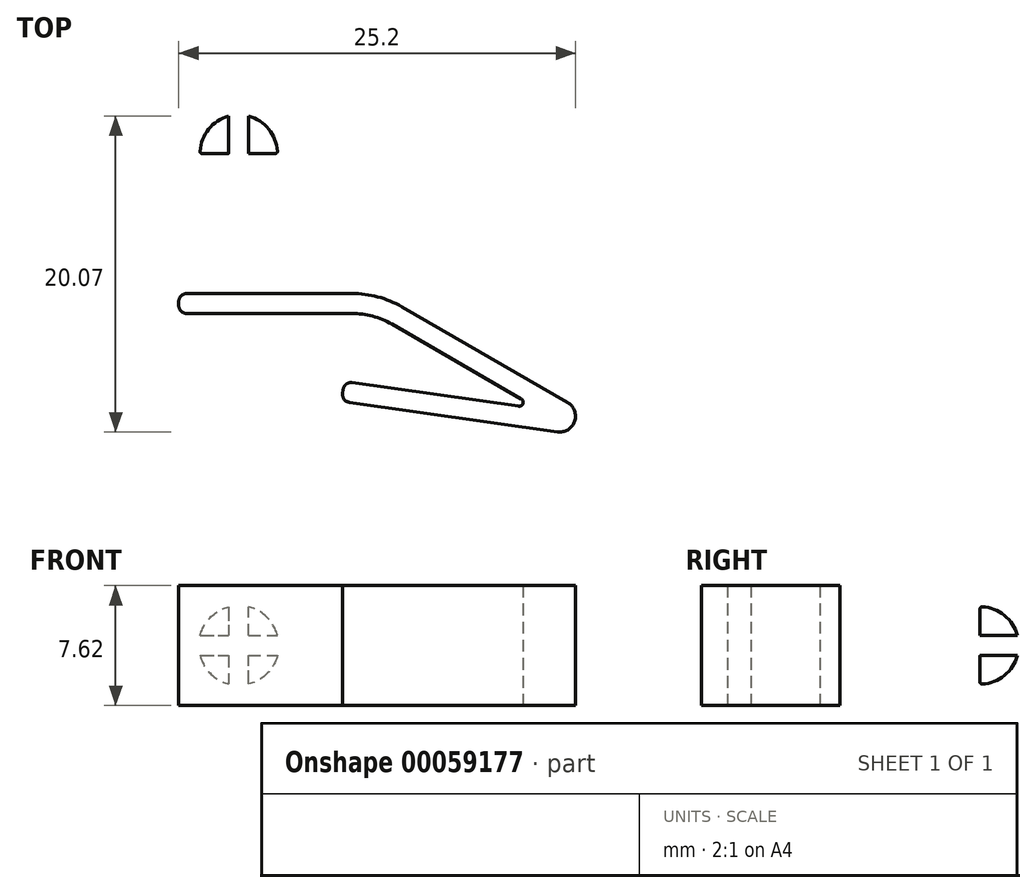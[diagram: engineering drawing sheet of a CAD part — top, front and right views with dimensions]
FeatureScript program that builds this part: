
annotation { "Feature Type Name" : "Feature", "Feature Type Description" : "" }
export const myFeature = defineFeature(function(context is Context, id is Id, definition is map)
    precondition{}
    {
        {
            var Q0;
            Q0=qCreatedBy(makeId("Top.planeOp"),FACE);
            var sketch = newSketch(context, id + "F0", { "sketchPlane" : qUnion([Q0])});
            skLineSegment(sketch, "E0", {"start": v(0.5, 0) * mm, "end": v(11, 0) * mm});
            skLineSegment(sketch, "E1", {"start": v(14.17, -0.85) * mm, "end": v(24.7, -6.93) * mm});
            skLineSegment(sketch, "E2", {"start": v(24.05, -8.8) * mm, "end": v(10.84, -6.92) * mm});
            skPoint(sketch, "E3.visualSharp", {"position": v(12.7, 0) * mm});
            skArc(sketch, "E3.filletArc", {"start": v(14.17, -0.85) * mm, "mid": v(12.64, -0.22) * mm, "end": v(11, 0) * mm});
            skPoint(sketch, "E4.visualSharp", {"position": v(29.2, -9.52) * mm});
            skArc(sketch, "E4.filletArc", {"start": v(24.05, -8.8) * mm, "mid": v(25.14, -8.13) * mm, "end": v(24.7, -6.93) * mm});
            skLineSegment(sketch, "E5.0", {"start": v(21.59, -7.16) * mm, "end": v(11.02, -5.66) * mm});
            skLineSegment(sketch, "E5.1", {"start": v(13.54, -1.95) * mm, "end": v(21.75, -6.7) * mm});
            skArc(sketch, "E5.2", {"start": v(13.54, -1.95) * mm, "mid": v(12.31, -1.44) * mm, "end": v(11, -1.27) * mm});
            skLineSegment(sketch, "E5.3", {"start": v(0.5, -1.27) * mm, "end": v(11, -1.27) * mm});
            skPoint(sketch, "E6.visualSharp", {"position": v(22.88, -7.35) * mm});
            skArc(sketch, "E6.filletArc", {"start": v(21.59, -7.16) * mm, "mid": v(21.86, -7) * mm, "end": v(21.75, -6.7) * mm});
            skLineSegment(sketch, "E7", {"start": v(0, -0.5) * mm, "end": v(0, -0.76) * mm});
            skLineSegment(sketch, "E8", {"start": v(10.44, -6.1) * mm, "end": v(10.4, -6.34) * mm});
            skPoint(sketch, "E9.visualSharp", {"position": v(10.52, -5.6) * mm});
            skArc(sketch, "E9.filletArc", {"start": v(11.02, -5.66) * mm, "mid": v(10.64, -5.76) * mm, "end": v(10.44, -6.1) * mm});
            skPoint(sketch, "E10.visualSharp", {"position": v(10.34, -6.85) * mm});
            skArc(sketch, "E10.filletArc", {"start": v(10.4, -6.34) * mm, "mid": v(10.5, -6.72) * mm, "end": v(10.84, -6.92) * mm});
            skPoint(sketch, "E11.visualSharp", {"position": v(0, 0) * mm});
            skArc(sketch, "E11.filletArc", {"start": v(0.5, 0) * mm, "mid": v(0.15, -0.15) * mm, "end": v(0, -0.5) * mm});
            skPoint(sketch, "E12.visualSharp", {"position": v(0, -1.27) * mm});
            skArc(sketch, "E12.filletArc", {"start": v(0, -0.76) * mm, "mid": v(0.15, -1.12) * mm, "end": v(0.5, -1.27) * mm});
            skSolve(sketch);
        }
        {
            var Q0;
            Q0=makeQuery(id+"F0.imprint","IMPRINT",FACE,{"disambiguationData":[TD([[makeQuery(id+"F0.imprint","IMPRINT",EDGE,{"derivedFrom":sQuery(id+"F0.wireOp",EDGE,"E0")}),-1.0]])]});
            extrude(context, id + "F1", {"entities" : qUnion([Q0]), "depth" : 7.62 * mm});
        }
        {
            var Q0;
            Q0=makeQuery(id+"F1.opExtrude","CAP_FACE",FACE,{"disambiguationData":[OSD([sQuery(id+"F0.wireOp",EDGE,"E0"),sQuery(id+"F0.wireOp",EDGE,"E1"),sQuery(id+"F0.wireOp",EDGE,"E2"),sQuery(id+"F0.wireOp",EDGE,"E3.filletArc"),sQuery(id+"F0.wireOp",EDGE,"E4.filletArc"),sQuery(id+"F0.wireOp",EDGE,"E5.0"),sQuery(id+"F0.wireOp",EDGE,"E5.1"),sQuery(id+"F0.wireOp",EDGE,"E5.2"),sQuery(id+"F0.wireOp",EDGE,"E5.3"),sQuery(id+"F0.wireOp",EDGE,"E6.filletArc"),sQuery(id+"F0.wireOp",EDGE,"E7"),sQuery(id+"F0.wireOp",EDGE,"E8"),sQuery(id+"F0.wireOp",EDGE,"E9.filletArc"),sQuery(id+"F0.wireOp",EDGE,"E10.filletArc"),sQuery(id+"F0.wireOp",EDGE,"E11.filletArc"),sQuery(id+"F0.wireOp",EDGE,"E12.filletArc")])],"isStart":false});
            cPlane(context, id + "F2", {"entities" : qUnion([Q0]), "cplaneType" : CPlaneType.OFFSET, "offset" : 3.8 * mm, "oppositeDirection" : true, "width" : 152.4 * mm, "height" : 152.4 * mm});
        }
        {
            var Q0;
            Q0=qCreatedBy(id+"F2.planeOp",FACE);
            var sketch = newSketch(context, id + "F3", { "sketchPlane" : qUnion([Q0])});
            skLineSegment(sketch, "E13", {"start": v(3.81, 0) * mm, "end": v(3.81, 8.9) * mm});
            skLineSegment(sketch, "E14", {"start": v(3.8, 8.9) * mm, "end": v(5.84, 8.9) * mm});
            skLineSegment(sketch, "E15", {"start": v(5.84, 8.9) * mm, "end": v(5.84, 0) * mm});
            skLineSegment(sketch, "E16", {"start": v(3.81, 0) * mm, "end": v(5.84, 0) * mm});
            skLineSegment(sketch, "E17", {"start": v(5.84, 8.9) * mm, "end": v(6.35, 8.9) * mm});
            skLineSegment(sketch, "E18", {"start": v(3.81, 8.9) * mm, "end": v(3.81, 12.2) * mm});
            skLineSegment(sketch, "E19.bottom", {"start": v(3.8, 3.05) * mm, "end": v(4.44, 3.05) * mm});
            skLineSegment(sketch, "E19.top", {"start": v(3.8, 12.2) * mm, "end": v(4.44, 12.2) * mm});
            skLineSegment(sketch, "E19.left", {"start": v(3.81, 3.05) * mm, "end": v(3.81, 12.2) * mm});
            skLineSegment(sketch, "E19.right", {"start": v(4.44, 3.05) * mm, "end": v(4.44, 12.2) * mm});
            skArc(sketch, "E20", {"start": v(6.35, 8.9) * mm, "mid": v(5.6, 10.69) * mm, "end": v(3.81, 11.43) * mm});
            skSolve(sketch);
        }
        {
            var Q0;
            Q0=makeQuery(id+"F3.imprint","IMPRINT",FACE,{"disambiguationData":[TD([[makeQuery(id+"F3.imprint","IMPRINT",EDGE,{"derivedFrom":sQuery(id+"F3.wireOp",EDGE,"E13")}),-1.0]])]});
            var Q1;
            {var subQ0=sQuery(id+"F3.wireOp",EDGE,"E17");Q1=makeQuery(id+"F3.imprint","IMPRINT",FACE,{"disambiguationData":[TD([[makeQuery(id+"F3.imprint","IMPRINT",EDGE,{"derivedFrom":subQ0}),1.0]])]});}
            var Q2;
            {var subQ0=sQuery(id+"F3.wireOp",EDGE,"E19.left");var subQ1=sQuery(id+"F3.wireOp",EDGE,"E14");var subQ2=makeQuery(id+"F3.imprint","INTERSECT",VERTEX,{"derivedFrom":[subQ1,subQ0]});Q2=makeQuery(id+"F3.imprint","IMPRINT",FACE,{"disambiguationData":[TD([[makeQuery(id+"F3.imprint","IMPRINT",EDGE,{"disambiguationData":[TD([[subQ2,-1.0]])],"derivedFrom":subQ1}),1.0]])]});}
            var Q3;
            {var subQ5=sQuery(id+"F3.wireOp",EDGE,"E19.bottom");Q3=makeQuery(id+"F3.imprint","IMPRINT",FACE,{"disambiguationData":[TD([[makeQuery(id+"F3.imprint","IMPRINT",EDGE,{"derivedFrom":subQ5}),1.0]])]});}
            var Q4;
            Q4=sQuery(id+"F3.wireOp",EDGE,"E13");
            revolve(context, id + "F4", {"operationType" : NewBodyOperationType.ADD, "entities" : qUnion([Q0, Q1, Q2, Q3]), "axis" : qUnion([Q4]), "revolveType" : RevolveType.FULL});
        }
        {
            var Q0;
            Q0=qCreatedBy(id+"F2.planeOp",FACE);
            var sketch = newSketch(context, id + "F5", { "sketchPlane" : qUnion([Q0])});
            skLineSegment(sketch, "E21.7", {"start": v(3.8, 3.05) * mm, "end": v(4.44, 3.05) * mm});
            skLineSegment(sketch, "E21.9", {"start": v(3.81, 3.05) * mm, "end": v(3.81, 13.2) * mm, "construction": true});
            skLineSegment(sketch, "E21.10", {"start": v(4.44, 3.05) * mm, "end": v(4.44, 13.2) * mm});
            skPoint(sketch, "E21.2.end.orphan", {"position": v(5.84, 0) * mm});
            skPoint(sketch, "E21.2.start.orphan", {"position": v(5.84, 8.9) * mm});
            skPoint(sketch, "E21.4.end.orphan", {"position": v(6.35, 8.9) * mm});
            skPoint(sketch, "E21.4.start.orphan", {"position": v(5.84, 8.9) * mm});
            skPoint(sketch, "E21.3.start.orphan", {"position": v(3.81, 0) * mm});
            skLineSegment(sketch, "E22.bottom", {"start": v(3.81, 3.05) * mm, "end": v(3.17, 3.05) * mm});
            skLineSegment(sketch, "E23", {"start": v(3.17, 13.2) * mm, "end": v(3.17, 3.05) * mm});
            skLineSegment(sketch, "E24", {"start": v(4.44, 13.2) * mm, "end": v(3.17, 13.2) * mm});
            skSolve(sketch);
        }
        {
            var Q0;
            {var subQ3=sQuery(id+"F5.wireOp",EDGE,"E21.7");Q0=makeQuery(id+"F5.imprint","IMPRINT",FACE,{"disambiguationData":[TD([[makeQuery(id+"F5.imprint","IMPRINT",EDGE,{"derivedFrom":subQ3}),1.0]])]});}
            extrude(context, id + "F6", {"entities" : qUnion([Q0]), "operationType" : NewBodyOperationType.REMOVE, "endBound" : BoundingType.SYMMETRIC, "oppositeDirection" : true, "depth" : 25.4 * mm});
        }
        {
            var Q0;
            {var subQ0=sQuery(id+"F3.wireOp",EDGE,"E17");var subQ1=sQuery(id+"F3.wireOp",EDGE,"16e9fac0-368d-41be-a28e-a698441af89b");Q0=makeQuery(id+"F6.boolean.opBoolean","SPLIT",EDGE,{"disambiguationData":[TD([makeQuery(id+"F6.opExtrude","SWEPT_FACE",FACE,{"disambiguationData":[OSD([sQuery(id+"F5.wireOp",EDGE,"E21.10")])]})])],"derivedFrom":makeQuery(id+"F4.opRevolve","SWEPT_EDGE",EDGE,{"disambiguationData":[OSD([subQ0,subQ1])]})});}
            var Q1;
            {var subQ0=sQuery(id+"F3.wireOp",EDGE,"E17");var subQ1=sQuery(id+"F3.wireOp",EDGE,"16e9fac0-368d-41be-a28e-a698441af89b");Q1=makeQuery(id+"F6.boolean.opBoolean","SPLIT",EDGE,{"disambiguationData":[TD([makeQuery(id+"F6.opExtrude","SWEPT_FACE",FACE,{"disambiguationData":[OSD([sQuery(id+"F5.wireOp",EDGE,"E23")])]})])],"derivedFrom":makeQuery(id+"F4.opRevolve","SWEPT_EDGE",EDGE,{"disambiguationData":[OSD([subQ0,subQ1])]})});}
            fillet(context, id + "F7", {"entities" : qUnion([Q0, Q1]), "radius" : 0.13 * mm, "tangentPropagation" : true, "allowEdgeOverflow" : false});
        }
        {
            var Q0;
            Q0=makeQuery(id+"F6.boolean.opBoolean","COPY",FACE,{"derivedFrom":makeQuery(id+"F6.opExtrude","SWEPT_FACE",FACE,{"disambiguationData":[OSD([sQuery(id+"F5.wireOp",EDGE,"E21.10")])]})});
            cPlane(context, id + "F8", {"entities" : qUnion([Q0]), "cplaneType" : CPlaneType.OFFSET, "offset" : 0.64 * mm, "width" : 152.4 * mm, "height" : 152.4 * mm});
        }
        {
            var Q0;
            Q0=qCreatedBy(id+"F8.planeOp",FACE);
            var sketch = newSketch(context, id + "F9", { "sketchPlane" : qUnion([Q0])});
            skLineSegment(sketch, "E25.0", {"start": v(-3.05, 1.88) * mm, "end": v(-3.05, 5.74) * mm, "construction": true});
            skLineSegment(sketch, "E26.bottom", {"start": v(-13.2, 4.45) * mm, "end": v(-3.05, 4.45) * mm});
            skLineSegment(sketch, "E26.top", {"start": v(-13.2, 3.17) * mm, "end": v(-3.05, 3.17) * mm});
            skLineSegment(sketch, "E26.left", {"start": v(-13.2, 4.45) * mm, "end": v(-13.2, 3.17) * mm});
            skLineSegment(sketch, "E26.right", {"start": v(-3.05, 4.45) * mm, "end": v(-3.05, 3.17) * mm, "construction": true});
            skLineSegment(sketch, "E27", {"start": v(-3.05, 4.45) * mm, "end": v(-3.05, 3.17) * mm});
            skSolve(sketch);
        }
        {
            var Q0;
            Q0=makeQuery(id+"F9.imprint","IMPRINT",FACE,{"disambiguationData":[TD([[makeQuery(id+"F9.imprint","IMPRINT",EDGE,{"derivedFrom":sQuery(id+"F9.wireOp",EDGE,"E26.bottom")}),-1.0]])]});
            extrude(context, id + "F10", {"entities" : qUnion([Q0]), "operationType" : NewBodyOperationType.REMOVE, "endBound" : BoundingType.SYMMETRIC, "oppositeDirection" : true, "depth" : 6.35 * mm});
        }
    });
